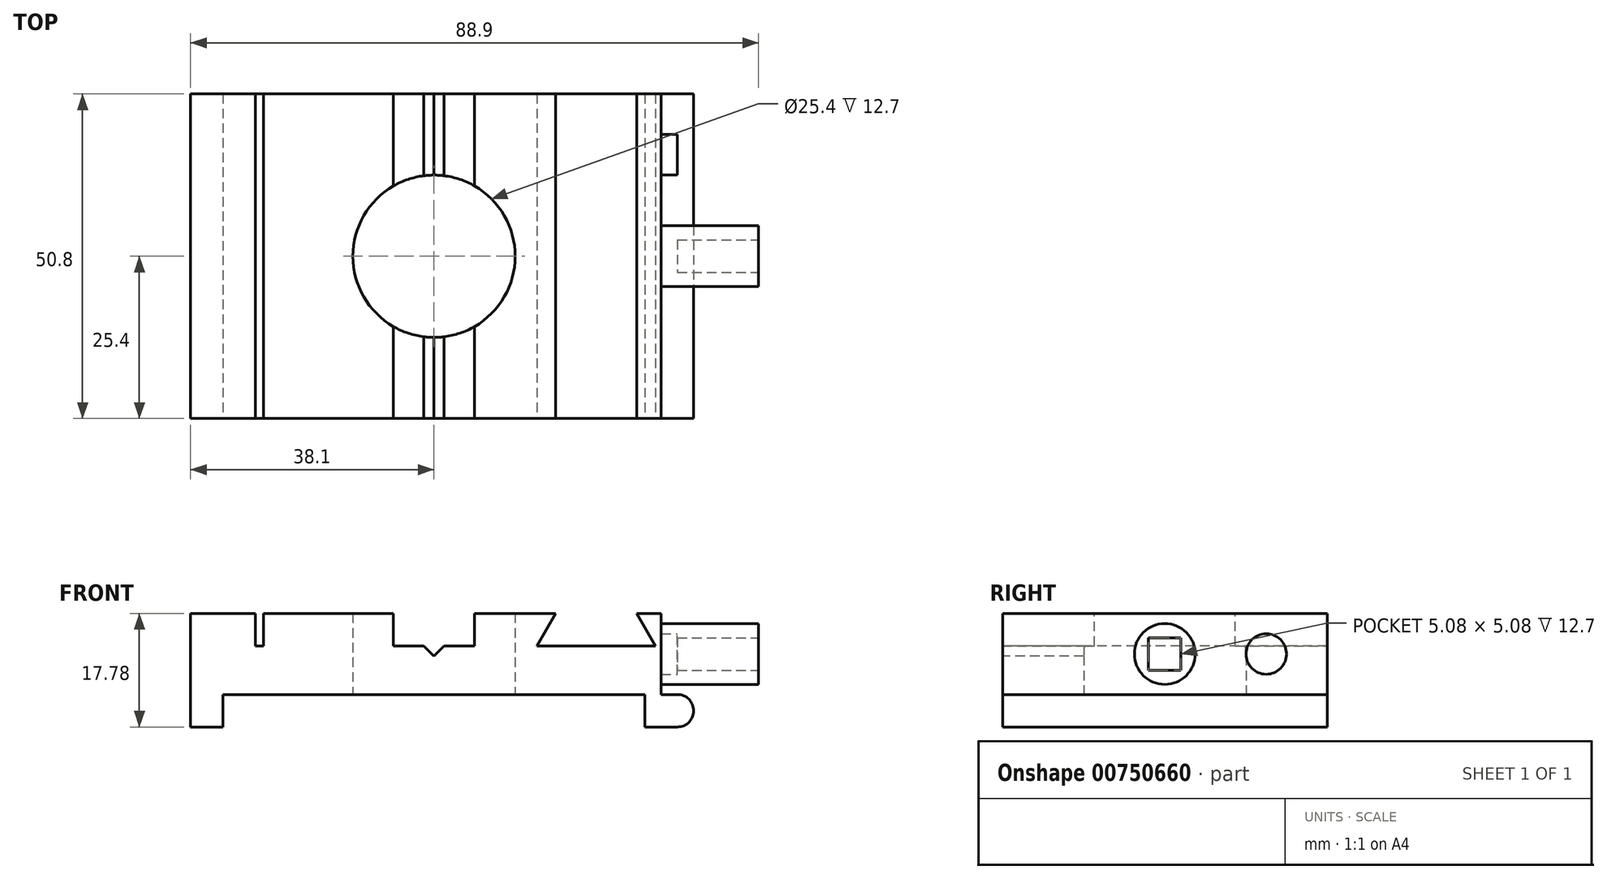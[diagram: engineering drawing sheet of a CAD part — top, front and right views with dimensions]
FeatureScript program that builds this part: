
annotation { "Feature Type Name" : "Feature", "Feature Type Description" : "" }
export const myFeature = defineFeature(function(context is Context, id is Id, definition is map)
    precondition{}
    {
        {
            var Q0;
            Q0=qCreatedBy(makeId("Top.planeOp"),FACE);
            var sketch = newSketch(context, id + "F0", { "sketchPlane" : qUnion([Q0])});
            skLineSegment(sketch, "E0.bottom", {"start": v(38.1, 25.4) * mm, "end": v(-38.1, 25.4) * mm});
            skLineSegment(sketch, "E0.top", {"start": v(38.1, -25.4) * mm, "end": v(-38.1, -25.4) * mm});
            skLineSegment(sketch, "E0.left", {"start": v(38.1, 25.4) * mm, "end": v(38.1, -25.4) * mm});
            skLineSegment(sketch, "E0.right", {"start": v(-38.1, 25.4) * mm, "end": v(-38.1, -25.4) * mm});
            skPoint(sketch, "E0.middle", {"position": v(0, 0) * mm});
            skCircle(sketch, "E1", {"center": v(0, 0) * mm, "radius": 12.7 * mm});
            skSolve(sketch);
        }
        {
            var Q0;
            Q0=makeQuery(id+"F0.imprint","IMPRINT",FACE,{"disambiguationData":[TD([[makeQuery(id+"F0.imprint","IMPRINT",EDGE,{"derivedFrom":sQuery(id+"F0.wireOp",EDGE,"E0.bottom")}),1.0]])]});
            extrude(context, id + "F1", {"entities" : qUnion([Q0]), "depth" : 12.7 * mm});
        }
        {
            var Q0;
            Q0=makeQuery(id+"F1.opExtrude","CAP_FACE",FACE,{"disambiguationData":[OSD([sQuery(id+"F0.wireOp",EDGE,"E0.bottom"),sQuery(id+"F0.wireOp",EDGE,"E0.top"),sQuery(id+"F0.wireOp",EDGE,"E0.left"),sQuery(id+"F0.wireOp",EDGE,"E0.right"),sQuery(id+"F0.wireOp",EDGE,"E1")])],"isStart":false});
            var sketch = newSketch(context, id + "F2", { "sketchPlane" : qUnion([Q0])});
            skLineSegment(sketch, "E2.bottom", {"start": v(-27.94, 25.4) * mm, "end": v(-26.67, 25.4) * mm});
            skLineSegment(sketch, "E2.top", {"start": v(-27.94, -25.4) * mm, "end": v(-26.67, -25.4) * mm});
            skLineSegment(sketch, "E2.left", {"start": v(-27.94, 25.4) * mm, "end": v(-27.94, -25.4) * mm});
            skLineSegment(sketch, "E2.right", {"start": v(-26.67, 25.4) * mm, "end": v(-26.67, -25.4) * mm});
            skLineSegment(sketch, "E3", {"start": v(-6.35, 25.4) * mm, "end": v(-6.35, -25.4) * mm});
            skLineSegment(sketch, "E4", {"start": v(-6.35, -25.4) * mm, "end": v(6.35, -25.4) * mm});
            skLineSegment(sketch, "E5", {"start": v(6.35, -25.4) * mm, "end": v(6.35, 25.4) * mm});
            skLineSegment(sketch, "E6", {"start": v(6.35, 25.4) * mm, "end": v(-6.35, 25.4) * mm});
            skPoint(sketch, "E7", {"position": v(0, 0) * mm});
            skLineSegment(sketch, "E8", {"start": v(0, 25.4) * mm, "end": v(0, -25.4) * mm, "construction": true});
            skSolve(sketch);
        }
        {
            var Q0;
            Q0=makeQuery(id+"F2.imprint","IMPRINT",FACE,{"disambiguationData":[TD([[makeQuery(id+"F2.imprint","IMPRINT",EDGE,{"derivedFrom":sQuery(id+"F2.wireOp",EDGE,"E2.bottom")}),1.0]])]});
            var Q1;
            {var subQ0=sQuery(id+"F2.wireOp",EDGE,"E4");Q1=makeQuery(id+"F2.imprint","IMPRINT",FACE,{"disambiguationData":[TD([[makeQuery(id+"F2.imprint","IMPRINT",EDGE,{"derivedFrom":subQ0}),-1.0]])]});}
            var Q2;
            {var subQ0=sQuery(id+"F2.wireOp",EDGE,"E6");Q2=makeQuery(id+"F2.imprint","IMPRINT",FACE,{"disambiguationData":[TD([[makeQuery(id+"F2.imprint","IMPRINT",EDGE,{"derivedFrom":subQ0}),1.0]])]});}
            extrude(context, id + "F3", {"entities" : qUnion([Q0, Q1, Q2]), "operationType" : NewBodyOperationType.REMOVE, "oppositeDirection" : true, "depth" : 5.08 * mm});
        }
        {
            var Q0;
            Q0=makeQuery(id+"F1.opExtrude","SWEPT_FACE",FACE,{"disambiguationData":[OSD([sQuery(id+"F0.wireOp",EDGE,"E0.top")])]});
            var sketch = newSketch(context, id + "F4", { "sketchPlane" : qUnion([Q0])});
            skLineSegment(sketch, "E9", {"start": v(19.05, 12.7) * mm, "end": v(16.12, 7.62) * mm});
            skLineSegment(sketch, "E10", {"start": v(16.12, 7.62) * mm, "end": v(34.68, 7.62) * mm});
            skLineSegment(sketch, "E11", {"start": v(34.68, 7.62) * mm, "end": v(31.75, 12.7) * mm});
            skLineSegment(sketch, "E12", {"start": v(31.75, 12.7) * mm, "end": v(19.05, 12.7) * mm});
            skLineSegment(sketch, "E13", {"start": v(25.4, 7.62) * mm, "end": v(25.4, 12.7) * mm, "construction": true});
            skSolve(sketch);
        }
        {
            var Q0;
            Q0=makeQuery(id+"F4.imprint","IMPRINT",FACE,{"disambiguationData":[TD([[makeQuery(id+"F4.imprint","IMPRINT",EDGE,{"derivedFrom":sQuery(id+"F4.wireOp",EDGE,"E9")}),1.0]])]});
            extrude(context, id + "F5", {"entities" : qUnion([Q0]), "operationType" : NewBodyOperationType.REMOVE, "endBound" : BoundingType.THROUGH_ALL, "oppositeDirection" : true, "depth" : 25.4 * mm});
        }
        {
            var Q0;
            Q0=makeQuery(id+"F1.opExtrude","SWEPT_FACE",FACE,{"disambiguationData":[OSD([sQuery(id+"F0.wireOp",EDGE,"E0.left")])]});
            var sketch = newSketch(context, id + "F6", { "sketchPlane" : qUnion([Q0])});
            skCircle(sketch, "E14", {"center": v(0, 6.35) * mm, "radius": 4.76 * mm});
            skPoint(sketch, "E14.centerSnap0", {"position": v(-25.4, 6.35) * mm});
            skPoint(sketch, "E14.centerSnap1", {"position": v(0, 12.7) * mm});
            skSolve(sketch);
        }
        {
            var Q0;
            Q0=makeQuery(id+"F6.imprint","IMPRINT",FACE,{"disambiguationData":[TD([[makeQuery(id+"F6.imprint","IMPRINT",EDGE,{"derivedFrom":sQuery(id+"F6.wireOp",EDGE,"E14")}),1.0]])]});
            extrude(context, id + "F7", {"entities" : qUnion([Q0]), "operationType" : NewBodyOperationType.ADD, "depth" : 12.7 * mm});
        }
        {
            var Q0;
            Q0=makeQuery(id+"F1.opExtrude","CAP_FACE",FACE,{"disambiguationData":[OSD([sQuery(id+"F0.wireOp",EDGE,"E0.bottom"),sQuery(id+"F0.wireOp",EDGE,"E0.top"),sQuery(id+"F0.wireOp",EDGE,"E0.left"),sQuery(id+"F0.wireOp",EDGE,"E0.right"),sQuery(id+"F0.wireOp",EDGE,"E1")])],"isStart":true});
            var sketch = newSketch(context, id + "F8", { "sketchPlane" : qUnion([Q0])});
            skLineSegment(sketch, "E15.bottom", {"start": v(38.1, -25.4) * mm, "end": v(33.02, -25.4) * mm});
            skLineSegment(sketch, "E15.top", {"start": v(38.1, 25.4) * mm, "end": v(33.02, 25.4) * mm});
            skLineSegment(sketch, "E15.left", {"start": v(38.1, -25.4) * mm, "end": v(38.1, 25.4) * mm});
            skLineSegment(sketch, "E15.right", {"start": v(33.02, -25.4) * mm, "end": v(33.02, 25.4) * mm});
            skLineSegment(sketch, "E16.bottom", {"start": v(-38.1, -25.4) * mm, "end": v(-33.02, -25.4) * mm});
            skLineSegment(sketch, "E16.top", {"start": v(-38.1, 25.4) * mm, "end": v(-33.02, 25.4) * mm});
            skLineSegment(sketch, "E16.left", {"start": v(-38.1, -25.4) * mm, "end": v(-38.1, 25.4) * mm});
            skLineSegment(sketch, "E16.right", {"start": v(-33.02, -25.4) * mm, "end": v(-33.02, 25.4) * mm});
            skSolve(sketch);
        }
        {
            var Q0;
            Q0=makeQuery(id+"F8.imprint","IMPRINT",FACE,{"disambiguationData":[TD([[makeQuery(id+"F8.imprint","IMPRINT",EDGE,{"derivedFrom":sQuery(id+"F8.wireOp",EDGE,"E16.bottom")}),-1.0]])]});
            var Q1;
            Q1=makeQuery(id+"F8.imprint","IMPRINT",FACE,{"disambiguationData":[TD([[makeQuery(id+"F8.imprint","IMPRINT",EDGE,{"derivedFrom":sQuery(id+"F8.wireOp",EDGE,"E15.bottom")}),-1.0]])]});
            extrude(context, id + "F9", {"entities" : qUnion([Q0, Q1]), "operationType" : NewBodyOperationType.ADD, "depth" : 5.08 * mm, "offsetDistance" : 25.4 * mm});
        }
        {
            var Q0;
            Q0=makeQuery(id+"F7.opExtrude","CAP_FACE",FACE,{"disambiguationData":[OSD([sQuery(id+"F6.wireOp",EDGE,"E14")])],"isStart":false});
            var sketch = newSketch(context, id + "F10", { "sketchPlane" : qUnion([Q0])});
            skLineSegment(sketch, "E17.bottom", {"start": v(2.54, 8.9) * mm, "end": v(-2.54, 8.9) * mm});
            skLineSegment(sketch, "E17.top", {"start": v(2.54, 3.81) * mm, "end": v(-2.54, 3.81) * mm});
            skLineSegment(sketch, "E17.left", {"start": v(2.54, 8.9) * mm, "end": v(2.54, 3.81) * mm});
            skLineSegment(sketch, "E17.right", {"start": v(-2.54, 8.9) * mm, "end": v(-2.54, 3.81) * mm});
            skPoint(sketch, "E17.middle", {"position": v(0, 6.35) * mm});
            skSolve(sketch);
        }
        {
            var Q0;
            Q0=makeQuery(id+"F10.imprint","IMPRINT",FACE,{"disambiguationData":[TD([[makeQuery(id+"F10.imprint","IMPRINT",EDGE,{"derivedFrom":sQuery(id+"F10.wireOp",EDGE,"E17.bottom")}),1.0]])]});
            extrude(context, id + "F11", {"entities" : qUnion([Q0]), "operationType" : NewBodyOperationType.REMOVE, "oppositeDirection" : true, "depth" : 12.7 * mm, "offsetDistance" : 25.4 * mm});
        }
        {
            var Q0;
            Q0=makeQuery(id+"F9.boolean.opBoolean","MERGE",FACE,{"derivedFrom":[makeQuery(id+"F1.opExtrude","SWEPT_FACE",FACE,{"disambiguationData":[OSD([sQuery(id+"F0.wireOp",EDGE,"E0.top")])]}),makeQuery(id+"F9.opExtrude","SWEPT_FACE",FACE,{"disambiguationData":[OSD([sQuery(id+"F8.wireOp",EDGE,"E15.top")])]}),makeQuery(id+"F9.opExtrude","SWEPT_FACE",FACE,{"disambiguationData":[OSD([sQuery(id+"F8.wireOp",EDGE,"E16.top")])]})]});
            var sketch = newSketch(context, id + "F12", { "sketchPlane" : qUnion([Q0])});
            skCircle(sketch, "E18", {"center": v(38.1, -2.54) * mm, "radius": 2.54 * mm});
            skLineSegment(sketch, "E19", {"start": v(38.1, 0) * mm, "end": v(38.1, -5.08) * mm});
            skSolve(sketch);
        }
        {
            var Q0;
            {var subQ0=sQuery(id+"F12.wireOp",EDGE,"E19");Q0=makeQuery(id+"F12.imprint","IMPRINT",FACE,{"disambiguationData":[TD([[makeQuery(id+"F12.imprint","IMPRINT",EDGE,{"derivedFrom":subQ0}),1.0]])]});}
            var Q1;
            Q1=makeQuery(id+"F9.boolean.opBoolean","MERGE",FACE,{"derivedFrom":[makeQuery(id+"F1.opExtrude","SWEPT_FACE",FACE,{"disambiguationData":[OSD([sQuery(id+"F0.wireOp",EDGE,"E0.bottom")])]}),makeQuery(id+"F9.opExtrude","SWEPT_FACE",FACE,{"disambiguationData":[OSD([sQuery(id+"F8.wireOp",EDGE,"E15.bottom")])]}),makeQuery(id+"F9.opExtrude","SWEPT_FACE",FACE,{"disambiguationData":[OSD([sQuery(id+"F8.wireOp",EDGE,"E16.bottom")])]})]});
            extrude(context, id + "F13", {"entities" : qUnion([Q0]), "operationType" : NewBodyOperationType.ADD, "endBound" : BoundingType.UP_TO_SURFACE, "oppositeDirection" : true, "depth" : 25.4 * mm, "endBoundEntityFace" : qUnion([Q1]), "offsetDistance" : 25.4 * mm});
        }
        {
            var Q0;
            Q0=makeQuery(id+"F9.boolean.opBoolean","MERGE",FACE,{"derivedFrom":[makeQuery(id+"F1.opExtrude","SWEPT_FACE",FACE,{"disambiguationData":[OSD([sQuery(id+"F0.wireOp",EDGE,"E0.left")])]}),makeQuery(id+"F9.opExtrude","SWEPT_FACE",FACE,{"disambiguationData":[OSD([sQuery(id+"F8.wireOp",EDGE,"E15.left")])]})]});
            var sketch = newSketch(context, id + "F14", { "sketchPlane" : qUnion([Q0])});
            skCircle(sketch, "E20.0", {"center": v(0, 6.35) * mm, "radius": 4.76 * mm});
            skCircle(sketch, "E21", {"center": v(-15.87, 6.35) * mm, "radius": 3.18 * mm});
            skLineSegment(sketch, "E22", {"start": v(0, 6.35) * mm, "end": v(0, -8.55) * mm, "construction": true});
            skCircle(sketch, "E23.MirrorC", {"center": v(15.88, 6.35) * mm, "radius": 3.18 * mm});
            skSolve(sketch);
        }
        {
            var Q0;
            Q0=makeQuery(id+"F14.imprint","IMPRINT",FACE,{"disambiguationData":[TD([[makeQuery(id+"F14.imprint","IMPRINT",EDGE,{"derivedFrom":sQuery(id+"F14.wireOp",EDGE,"E21")}),1.0]])]});
            var Q1;
            Q1=makeQuery(id+"F14.imprint","IMPRINT",FACE,{"disambiguationData":[TD([[makeQuery(id+"F14.imprint","IMPRINT",EDGE,{"derivedFrom":sQuery(id+"F14.wireOp",EDGE,"E23.MirrorC")}),-1.0]])]});
            extrude(context, id + "F15", {"entities" : qUnion([Q0, Q1]), "operationType" : NewBodyOperationType.REMOVE, "oppositeDirection" : true, "depth" : 2.54 * mm, "offsetDistance" : 25.4 * mm});
        }
        {
            var Q0;
            {var subQ0=sQuery(id+"F12.wireOp",EDGE,"E19");var subQ1=sQuery(id+"F12.wireOp",EDGE,"E18");Q0=makeQuery(id+"FixT509f4eRxLjC_1.1.F13.boolean.opBoolean","MERGE",FACE,{"derivedFrom":[makeQuery(id+"F13.boolean.opBoolean","MERGE",FACE,{"derivedFrom":[makeQuery(id+"F9.boolean.opBoolean","MERGE",FACE,{"derivedFrom":[makeQuery(id+"F1.opExtrude","SWEPT_FACE",FACE,{"disambiguationData":[OSD([sQuery(id+"F0.wireOp",EDGE,"E0.top")])]}),makeQuery(id+"F9.opExtrude","SWEPT_FACE",FACE,{"disambiguationData":[OSD([sQuery(id+"F8.wireOp",EDGE,"E15.top")])]}),makeQuery(id+"F9.opExtrude","SWEPT_FACE",FACE,{"disambiguationData":[OSD([sQuery(id+"F8.wireOp",EDGE,"E16.top")])]})]}),makeQuery(id+"F13.opExtrude","CAP_FACE",FACE,{"disambiguationData":[OSD([subQ1,subQ0])],"isStart":true})]}),makeQuery(id+"FixT509f4eRxLjC_1.1.F13.opExtrude","CAP_FACE",FACE,{"disambiguationData":[OSD([subQ1,subQ0])],"isStart":true})]});}
            var sketch = newSketch(context, id + "F16", { "sketchPlane" : qUnion([Q0])});
            skLineSegment(sketch, "E24", {"start": v(0, 7.62) * mm, "end": v(0, -7.62) * mm, "construction": true});
            skLineSegment(sketch, "E25", {"start": v(0, 6.03) * mm, "end": v(1.59, 7.62) * mm});
            skLineSegment(sketch, "E26", {"start": v(1.59, 7.62) * mm, "end": v(-1.59, 7.62) * mm});
            skLineSegment(sketch, "E27", {"start": v(-1.59, 7.62) * mm, "end": v(0, 6.03) * mm});
            skSolve(sketch);
        }
        {
            var Q0;
            Q0=makeQuery(id+"F16.imprint","IMPRINT",FACE,{"disambiguationData":[TD([[makeQuery(id+"F16.imprint","IMPRINT",EDGE,{"derivedFrom":sQuery(id+"F16.wireOp",EDGE,"E25")}),1.0]])]});
            extrude(context, id + "F17", {"entities" : qUnion([Q0]), "operationType" : NewBodyOperationType.REMOVE, "endBound" : BoundingType.THROUGH_ALL, "oppositeDirection" : true, "depth" : 25.4 * mm, "offsetDistance" : 25.4 * mm});
        }
    });
